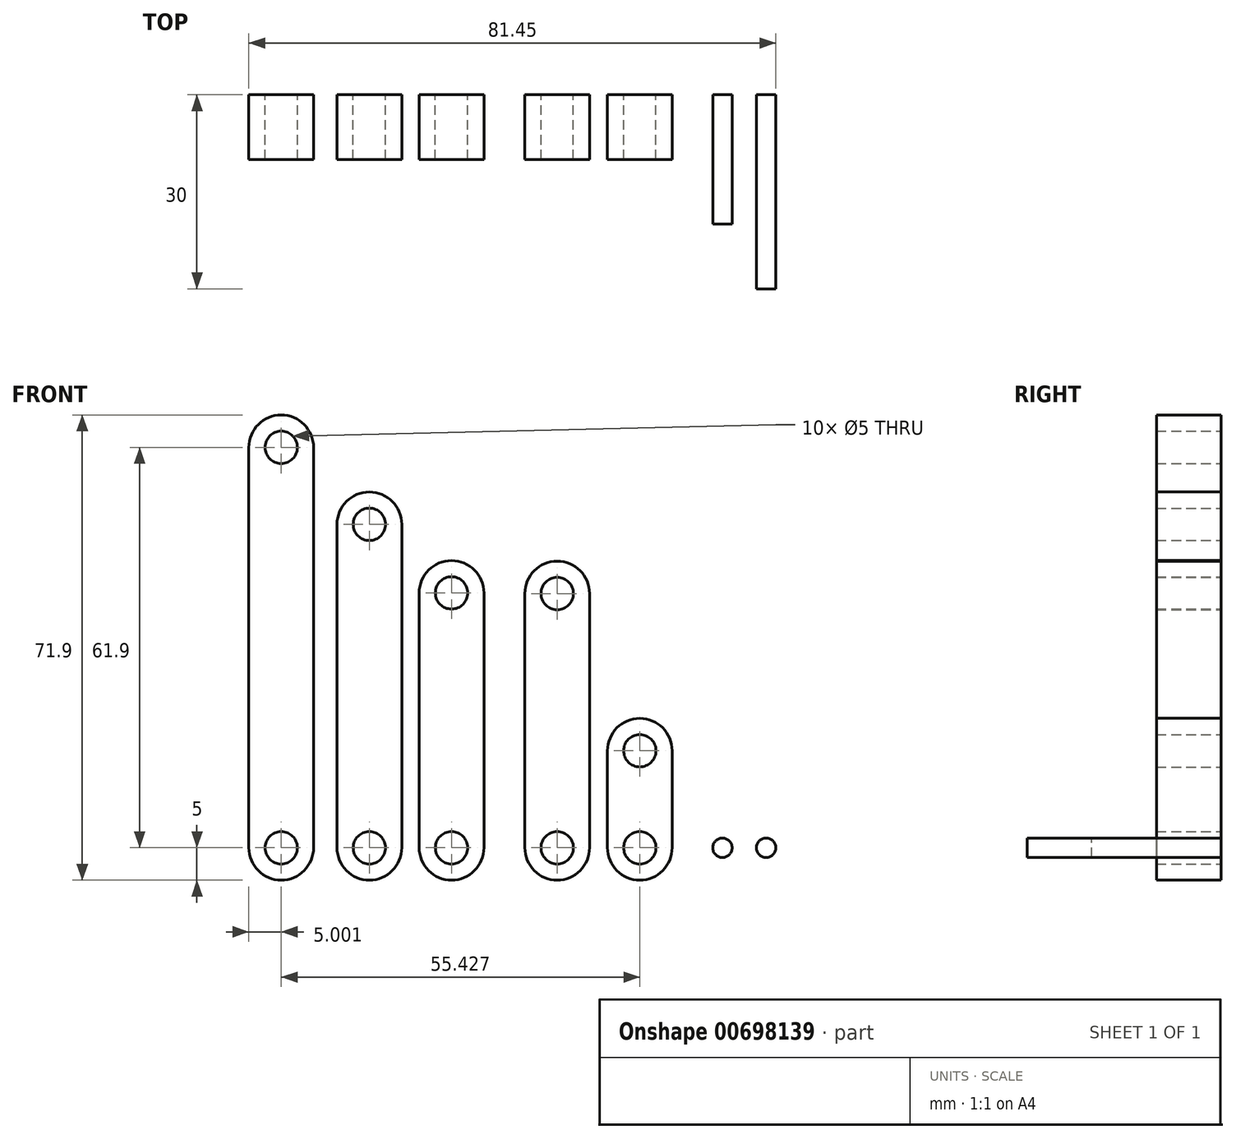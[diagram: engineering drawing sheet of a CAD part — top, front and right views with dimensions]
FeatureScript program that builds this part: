
annotation { "Feature Type Name" : "Feature", "Feature Type Description" : "" }
export const myFeature = defineFeature(function(context is Context, id is Id, definition is map)
    precondition{}
    {
        {
            assignVariable(context, id + "F0", {"name" : "thinkness", "anyValue" : 10});
        }
        {
            var Q0;
            Q0=qCreatedBy(makeId("Front.planeOp"),FACE);
            var sketch = newSketch(context, id + "F1", { "sketchPlane" : qUnion([Q0])});
            skArc(sketch, "E0", {"start": v(-17.77, 0) * mm, "mid": v(-12.77, -5) * mm, "end": v(-7.77, 0) * mm});
            skArc(sketch, "E1", {"start": v(-7.77, 15) * mm, "mid": v(-12.77, 20) * mm, "end": v(-17.77, 15) * mm});
            skLineSegment(sketch, "E2", {"start": v(-17.77, 15) * mm, "end": v(-17.77, 0) * mm});
            skLineSegment(sketch, "E3", {"start": v(-7.77, 0) * mm, "end": v(-7.77, 15) * mm});
            skCircle(sketch, "E4", {"center": v(-12.77, 15) * mm, "radius": 2.5 * mm});
            skCircle(sketch, "E5", {"center": v(-12.77, 0) * mm, "radius": 2.5 * mm});
            skSolve(sketch);
        }
        {
            var Q0;
            Q0=makeQuery(id+"F1.imprint","IMPRINT",FACE,{"disambiguationData":[TD([[makeQuery(id+"F1.imprint","IMPRINT",EDGE,{"derivedFrom":sQuery(id+"F1.wireOp",EDGE,"E0")}),1.0]])]});
            extrude(context, id + "F2", {"entities" : qUnion([Q0]), "depth" : (getVariable(context, 'thinkness')) * mm, "offsetDistance" : 25 * mm});
        }
        {
            var Q0;
            Q0=qCreatedBy(makeId("Front.planeOp"),FACE);
            var sketch = newSketch(context, id + "F3", { "sketchPlane" : qUnion([Q0])});
            skArc(sketch, "E6", {"start": v(-30.54, 0) * mm, "mid": v(-25.54, -5) * mm, "end": v(-20.54, 0) * mm});
            skArc(sketch, "E7", {"start": v(-20.54, 39.3) * mm, "mid": v(-25.54, 44.3) * mm, "end": v(-30.54, 39.3) * mm});
            skLineSegment(sketch, "E8", {"start": v(-30.54, 39.3) * mm, "end": v(-30.54, 0) * mm});
            skLineSegment(sketch, "E9", {"start": v(-20.54, 0) * mm, "end": v(-20.54, 39.3) * mm});
            skCircle(sketch, "E10", {"center": v(-25.54, 39.3) * mm, "radius": 2.5 * mm});
            skCircle(sketch, "E11", {"center": v(-25.54, 0) * mm, "radius": 2.5 * mm});
            skSolve(sketch);
        }
        {
            var Q0;
            Q0=makeQuery(id+"F3.imprint","IMPRINT",FACE,{"disambiguationData":[TD([[makeQuery(id+"F3.imprint","IMPRINT",EDGE,{"derivedFrom":sQuery(id+"F3.wireOp",EDGE,"E6")}),1.0]])]});
            extrude(context, id + "F4", {"entities" : qUnion([Q0]), "depth" : (getVariable(context, 'thinkness')) * mm, "offsetDistance" : 25 * mm});
        }
        {
            var Q0;
            Q0=qCreatedBy(makeId("Front.planeOp"),FACE);
            var sketch = newSketch(context, id + "F5", { "sketchPlane" : qUnion([Q0])});
            skArc(sketch, "E12", {"start": v(-46.88, 0) * mm, "mid": v(-41.88, -5) * mm, "end": v(-36.88, 0) * mm});
            skArc(sketch, "E13", {"start": v(-36.88, 39.4) * mm, "mid": v(-41.88, 44.4) * mm, "end": v(-46.88, 39.4) * mm});
            skLineSegment(sketch, "E14", {"start": v(-46.88, 39.4) * mm, "end": v(-46.88, 0) * mm});
            skLineSegment(sketch, "E15", {"start": v(-36.88, 0) * mm, "end": v(-36.88, 39.4) * mm});
            skCircle(sketch, "E16", {"center": v(-41.88, 39.4) * mm, "radius": 2.5 * mm});
            skCircle(sketch, "E17", {"center": v(-41.88, 0) * mm, "radius": 2.5 * mm});
            skSolve(sketch);
        }
        {
            var Q0;
            Q0=makeQuery(id+"F5.imprint","IMPRINT",FACE,{"disambiguationData":[TD([[makeQuery(id+"F5.imprint","IMPRINT",EDGE,{"derivedFrom":sQuery(id+"F5.wireOp",EDGE,"E12")}),1.0]])]});
            extrude(context, id + "F6", {"entities" : qUnion([Q0]), "depth" : (getVariable(context, 'thinkness')) * mm, "offsetDistance" : 25 * mm});
        }
        {
            var Q0;
            Q0=qCreatedBy(makeId("Front.planeOp"),FACE);
            var sketch = newSketch(context, id + "F7", { "sketchPlane" : qUnion([Q0])});
            skArc(sketch, "E18", {"start": v(-59.57, 0) * mm, "mid": v(-54.57, -5) * mm, "end": v(-49.57, 0) * mm});
            skArc(sketch, "E19", {"start": v(-49.57, 50) * mm, "mid": v(-54.57, 55) * mm, "end": v(-59.57, 50) * mm});
            skLineSegment(sketch, "E20", {"start": v(-59.57, 50) * mm, "end": v(-59.57, 0) * mm});
            skLineSegment(sketch, "E21", {"start": v(-49.57, 0) * mm, "end": v(-49.57, 50) * mm});
            skCircle(sketch, "E22", {"center": v(-54.57, 50) * mm, "radius": 2.5 * mm});
            skCircle(sketch, "E23", {"center": v(-54.57, 0) * mm, "radius": 2.5 * mm});
            skSolve(sketch);
        }
        {
            var Q0;
            Q0=makeQuery(id+"F7.imprint","IMPRINT",FACE,{"disambiguationData":[TD([[makeQuery(id+"F7.imprint","IMPRINT",EDGE,{"derivedFrom":sQuery(id+"F7.wireOp",EDGE,"E18")}),1.0]])]});
            extrude(context, id + "F8", {"entities" : qUnion([Q0]), "depth" : (getVariable(context, 'thinkness')) * mm, "offsetDistance" : 25 * mm});
        }
        {
            var Q0;
            Q0=qCreatedBy(makeId("Front.planeOp"),FACE);
            var sketch = newSketch(context, id + "F9", { "sketchPlane" : qUnion([Q0])});
            skArc(sketch, "E24", {"start": v(-73.2, 0) * mm, "mid": v(-68.2, -5) * mm, "end": v(-63.2, 0) * mm});
            skArc(sketch, "E25", {"start": v(-63.2, 61.9) * mm, "mid": v(-68.2, 66.9) * mm, "end": v(-73.2, 61.9) * mm});
            skLineSegment(sketch, "E26", {"start": v(-73.2, 61.9) * mm, "end": v(-73.2, 0) * mm});
            skLineSegment(sketch, "E27", {"start": v(-63.2, 0) * mm, "end": v(-63.2, 61.9) * mm});
            skCircle(sketch, "E28", {"center": v(-68.2, 61.9) * mm, "radius": 2.5 * mm});
            skCircle(sketch, "E29", {"center": v(-68.2, 0) * mm, "radius": 2.5 * mm});
            skSolve(sketch);
        }
        {
            var Q0;
            Q0=makeQuery(id+"F9.imprint","IMPRINT",FACE,{"disambiguationData":[TD([[makeQuery(id+"F9.imprint","IMPRINT",EDGE,{"derivedFrom":sQuery(id+"F9.wireOp",EDGE,"E24")}),1.0]])]});
            extrude(context, id + "F10", {"entities" : qUnion([Q0]), "depth" : (getVariable(context, 'thinkness')) * mm, "offsetDistance" : 25 * mm});
        }
        {
            var Q0;
            Q0=qCreatedBy(makeId("Front.planeOp"),FACE);
            var sketch = newSketch(context, id + "F11", { "sketchPlane" : qUnion([Q0])});
            skCircle(sketch, "E30", {"center": v(0, 0) * mm, "radius": 1.5 * mm});
            skSolve(sketch);
        }
        {
            var Q0;
            Q0=qSketchRegion(id+"F11",true);
            extrude(context, id + "F12", {"entities" : qUnion([Q0]), "depth" : (getVariable(context, 'thinkness') * 2) * mm, "offsetDistance" : 25 * mm});
        }
        {
            var Q0;
            Q0=qCreatedBy(makeId("Front.planeOp"),FACE);
            var sketch = newSketch(context, id + "F13", { "sketchPlane" : qUnion([Q0])});
            skCircle(sketch, "E31", {"center": v(6.75, 0) * mm, "radius": 1.5 * mm});
            skSolve(sketch);
        }
        {
            var Q0;
            Q0=makeQuery(id+"F13.imprint","IMPRINT",FACE,{"disambiguationData":[TD([[makeQuery(id+"F13.imprint","IMPRINT",EDGE,{"derivedFrom":sQuery(id+"F13.wireOp",EDGE,"E31")}),1.0]])]});
            extrude(context, id + "F14", {"entities" : qUnion([Q0]), "depth" : (getVariable(context, 'thinkness') * 3) * mm, "offsetDistance" : 25 * mm});
        }
    });
